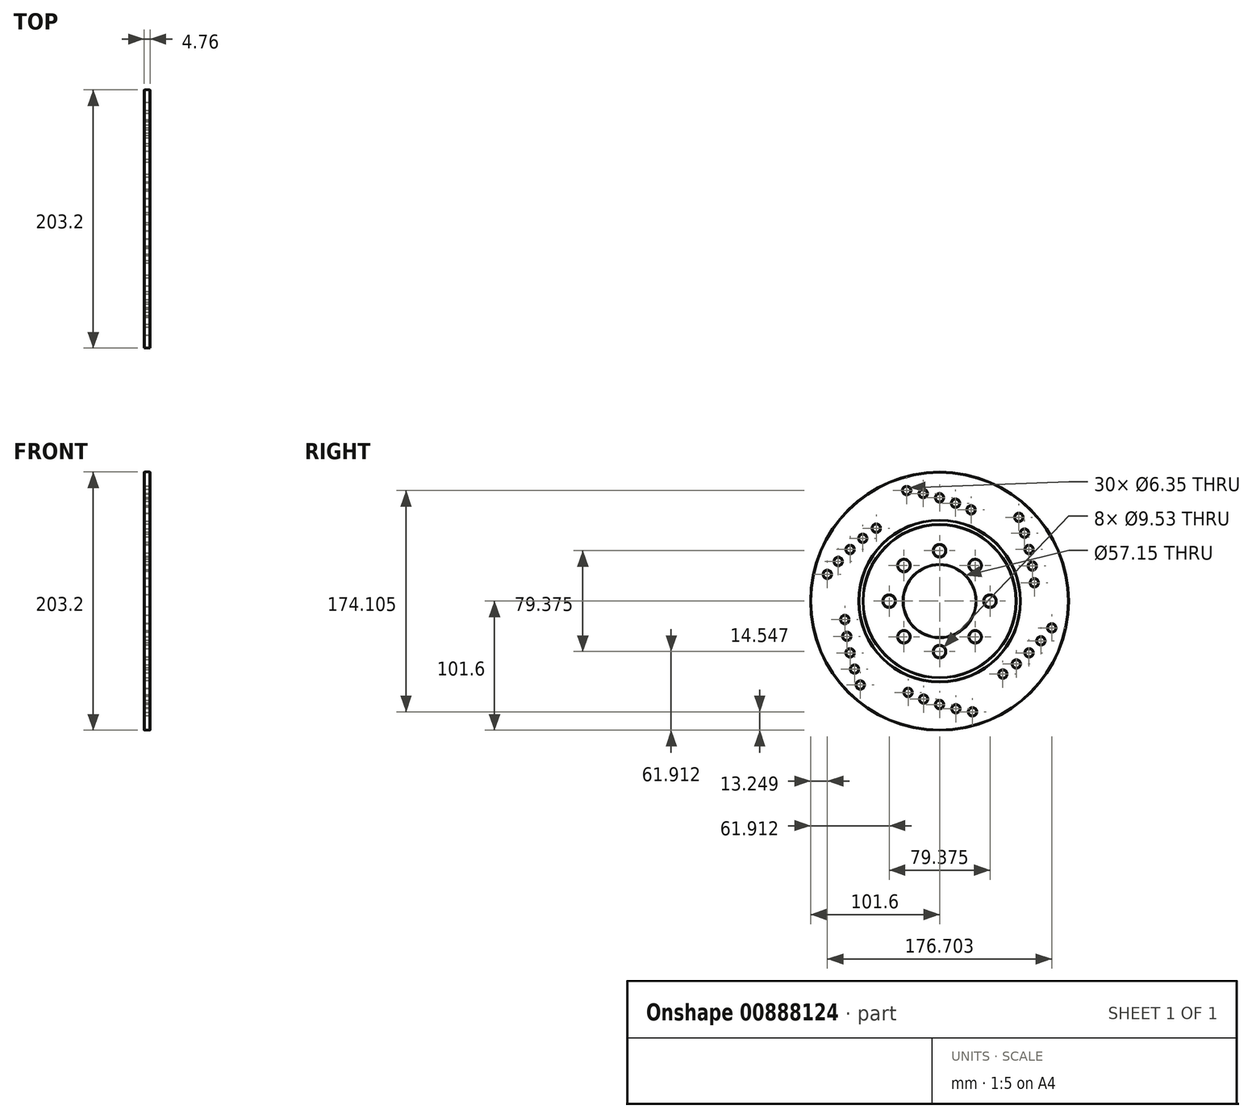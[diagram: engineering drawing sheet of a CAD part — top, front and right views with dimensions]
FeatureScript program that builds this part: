
annotation { "Feature Type Name" : "Feature", "Feature Type Description" : "" }
export const myFeature = defineFeature(function(context is Context, id is Id, definition is map)
    precondition{}
    {
        {
            var Q0;
            Q0=qCreatedBy(makeId("Right.planeOp"),FACE);
            var sketch = newSketch(context, id + "F0", { "sketchPlane" : qUnion([Q0])});
            skCircle(sketch, "E0", {"center": v(0, 0) * mm, "radius": 28.58 * mm});
            skCircle(sketch, "E1", {"center": v(0, 0) * mm, "radius": 101.6 * mm});
            skLineSegment(sketch, "E2", {"start": v(0, 0) * mm, "end": v(0, 39.69) * mm, "construction": true});
            skCircle(sketch, "E3", {"center": v(0, 39.69) * mm, "radius": 4.76 * mm});
            skCircle(sketch, "E4.1.0", {"center": v(-28.06, 28.06) * mm, "radius": 4.76 * mm});
            skCircle(sketch, "E4.2.0", {"center": v(-39.69, 0) * mm, "radius": 4.76 * mm});
            skCircle(sketch, "E4.3.0", {"center": v(-28.06, -28.06) * mm, "radius": 4.76 * mm});
            skCircle(sketch, "E4.4.0", {"center": v(0, -39.69) * mm, "radius": 4.76 * mm});
            skCircle(sketch, "E4.5.0", {"center": v(28.06, -28.06) * mm, "radius": 4.76 * mm});
            skCircle(sketch, "E4.6.0", {"center": v(39.69, 0) * mm, "radius": 4.76 * mm});
            skCircle(sketch, "E4.7.0", {"center": v(28.06, 28.06) * mm, "radius": 4.76 * mm});
            skLineSegment(sketch, "E5", {"start": v(0, 39.69) * mm, "end": v(0, 81.36) * mm, "construction": true});
            skArc(sketch, "E6", {"start": v(24.78, 71.84) * mm, "mid": v(0, 81.36) * mm, "end": v(-25.92, 87.05) * mm, "construction": true});
            skCircle(sketch, "E7", {"center": v(-25.92, 87.05) * mm, "radius": 3.18 * mm});
            skCircle(sketch, "E8", {"center": v(24.78, 71.84) * mm, "radius": 3.18 * mm});
            skCircle(sketch, "E9", {"center": v(0, 81.36) * mm, "radius": 3.18 * mm});
            skCircle(sketch, "E10", {"center": v(-12.85, 84.7) * mm, "radius": 3.18 * mm});
            skCircle(sketch, "E11", {"center": v(12.57, 77.07) * mm, "radius": 3.18 * mm});
            skLineSegment(sketch, "E12", {"start": v(-25.92, 87.05) * mm, "end": v(-12.85, 84.7) * mm, "construction": true});
            skLineSegment(sketch, "E13", {"start": v(-12.85, 84.7) * mm, "end": v(0, 81.36) * mm, "construction": true});
            skLineSegment(sketch, "E14", {"start": v(0, 81.36) * mm, "end": v(12.57, 77.07) * mm, "construction": true});
            skLineSegment(sketch, "E15", {"start": v(0, 0) * mm, "end": v(-50.8, -87.99) * mm, "construction": true});
            skCircle(sketch, "E16.1.0", {"center": v(-88.35, 21.08) * mm, "radius": 3.18 * mm});
            skCircle(sketch, "E16.1.1", {"center": v(-79.77, 31.21) * mm, "radius": 3.18 * mm});
            skCircle(sketch, "E16.1.2", {"center": v(-70.46, 40.68) * mm, "radius": 3.18 * mm});
            skCircle(sketch, "E16.1.3", {"center": v(-60.46, 49.42) * mm, "radius": 3.18 * mm});
            skCircle(sketch, "E16.1.4", {"center": v(-49.83, 57.38) * mm, "radius": 3.18 * mm});
            skCircle(sketch, "E16.2.0", {"center": v(-62.43, -65.98) * mm, "radius": 3.18 * mm});
            skCircle(sketch, "E16.2.1", {"center": v(-66.92, -53.48) * mm, "radius": 3.18 * mm});
            skCircle(sketch, "E16.2.2", {"center": v(-70.46, -40.68) * mm, "radius": 3.18 * mm});
            skCircle(sketch, "E16.2.3", {"center": v(-73.02, -27.65) * mm, "radius": 3.18 * mm});
            skCircle(sketch, "E16.2.4", {"center": v(-74.6, -14.46) * mm, "radius": 3.18 * mm});
            skCircle(sketch, "E16.3.0", {"center": v(25.92, -87.05) * mm, "radius": 3.18 * mm});
            skCircle(sketch, "E16.3.1", {"center": v(12.85, -84.7) * mm, "radius": 3.18 * mm});
            skCircle(sketch, "E16.3.2", {"center": v(0, -81.36) * mm, "radius": 3.18 * mm});
            skCircle(sketch, "E16.3.3", {"center": v(-12.57, -77.07) * mm, "radius": 3.18 * mm});
            skCircle(sketch, "E16.3.4", {"center": v(-24.78, -71.84) * mm, "radius": 3.18 * mm});
            skCircle(sketch, "E16.4.0", {"center": v(88.35, -21.08) * mm, "radius": 3.18 * mm});
            skCircle(sketch, "E16.4.1", {"center": v(79.77, -31.21) * mm, "radius": 3.18 * mm});
            skCircle(sketch, "E16.4.2", {"center": v(70.46, -40.68) * mm, "radius": 3.18 * mm});
            skCircle(sketch, "E16.4.3", {"center": v(60.46, -49.42) * mm, "radius": 3.18 * mm});
            skCircle(sketch, "E16.4.4", {"center": v(49.83, -57.38) * mm, "radius": 3.18 * mm});
            skCircle(sketch, "E16.5.0", {"center": v(62.43, 65.98) * mm, "radius": 3.18 * mm});
            skCircle(sketch, "E16.5.1", {"center": v(66.92, 53.48) * mm, "radius": 3.18 * mm});
            skCircle(sketch, "E16.5.2", {"center": v(70.46, 40.68) * mm, "radius": 3.18 * mm});
            skCircle(sketch, "E16.5.3", {"center": v(73.02, 27.65) * mm, "radius": 3.18 * mm});
            skCircle(sketch, "E16.5.4", {"center": v(74.6, 14.46) * mm, "radius": 3.18 * mm});
            skSolve(sketch);
        }
        {
            var Q0;
            Q0 = qSketchRegion(id + "F0", true);
            extrude(context, id + "F1", {"entities" : qUnion([Q0]), "depth" : 4.76 * mm, "offsetDistance" : 25.4 * mm, "symmetric" : true});
        }
        {
            var Q0;
            Q0=qCreatedBy(makeId("Front.planeOp"),FACE);
            var sketch = newSketch(context, id + "F2", { "sketchPlane" : qUnion([Q0])});
            skLineSegment(sketch, "E17", {"start": v(0, 0) * mm, "end": v(-25.4, 0) * mm, "construction": true});
            skLineSegment(sketch, "E18.bottom", {"start": v(-2.13, 63.5) * mm, "end": v(-25.4, 63.5) * mm});
            skLineSegment(sketch, "E18.top", {"start": v(-2.13, 60.33) * mm, "end": v(-25.4, 60.33) * mm});
            skLineSegment(sketch, "E18.left", {"start": v(-2.13, 63.5) * mm, "end": v(-2.13, 60.33) * mm});
            skLineSegment(sketch, "E18.right", {"start": v(-25.4, 63.5) * mm, "end": v(-25.4, 60.33) * mm});
            skLineSegment(sketch, "E19", {"start": v(0, 0) * mm, "end": v(0, 25.4) * mm, "construction": true});
            skLineSegment(sketch, "E20.MirrorCS", {"start": v(2.13, 63.5) * mm, "end": v(2.13, 60.33) * mm});
            skLineSegment(sketch, "E21.MirrorCS", {"start": v(2.13, 63.5) * mm, "end": v(25.4, 63.5) * mm});
            skLineSegment(sketch, "E22.MirrorCS", {"start": v(25.4, 63.5) * mm, "end": v(25.4, 60.33) * mm});
            skLineSegment(sketch, "E23.MirrorCS", {"start": v(2.13, 60.33) * mm, "end": v(25.4, 60.33) * mm});
            skSolve(sketch);
        }
        {
            var Q0;
            Q0=makeQuery(id+"F2.imprint","IMPRINT",FACE,{"disambiguationData":[TD([[makeQuery(id+"F2.imprint","IMPRINT",EDGE,{"derivedFrom":sQuery(id+"F2.wireOp",EDGE,"E18.bottom")}),1.0]])]});
            var Q1;
            Q1=makeQuery(id+"F2.imprint","IMPRINT",FACE,{"disambiguationData":[TD([[makeQuery(id+"F2.imprint","IMPRINT",EDGE,{"derivedFrom":sQuery(id+"F2.wireOp",EDGE,"E20.MirrorCS")}),1.0]])]});
            var Q2;
            Q2=sQuery(id+"F2.wireOp",EDGE,"E17");
            revolve(context, id + "F3", {"operationType" : NewBodyOperationType.REMOVE, "surfaceOperationType" : NewSurfaceOperationType.NEW, "entities" : qUnion([Q0, Q1]), "axis" : qUnion([Q2]), "revolveType" : RevolveType.FULL, "oppositeDirection" : true});
        }
        {
            var Q0;
            {var subQ0=sQuery(id+"F0.wireOp",EDGE,"E16.4.0");var subQ1=sQuery(id+"F0.wireOp",EDGE,"E16.3.4");var subQ2=sQuery(id+"F0.wireOp",EDGE,"E16.3.3");var subQ3=sQuery(id+"F0.wireOp",EDGE,"E16.3.2");var subQ4=sQuery(id+"F0.wireOp",EDGE,"E16.3.1");var subQ5=sQuery(id+"F0.wireOp",EDGE,"E16.3.0");var subQ6=sQuery(id+"F0.wireOp",EDGE,"E16.2.3");var subQ7=sQuery(id+"F0.wireOp",EDGE,"E16.2.2");var subQ8=sQuery(id+"F0.wireOp",EDGE,"E16.2.1");var subQ9=sQuery(id+"F0.wireOp",EDGE,"E16.2.0");var subQ10=sQuery(id+"F0.wireOp",EDGE,"E16.1.4");var subQ11=sQuery(id+"F0.wireOp",EDGE,"E9");var subQ12=sQuery(id+"F0.wireOp",EDGE,"E16.2.4");var subQ13=sQuery(id+"F0.wireOp",EDGE,"E1");var subQ14=sQuery(id+"F0.wireOp",EDGE,"E7");var subQ15=sQuery(id+"F0.wireOp",EDGE,"E8");var subQ16=sQuery(id+"F0.wireOp",EDGE,"E10");var subQ17=sQuery(id+"F0.wireOp",EDGE,"E11");var subQ18=sQuery(id+"F0.wireOp",EDGE,"E16.1.0");var subQ19=sQuery(id+"F0.wireOp",EDGE,"E16.1.1");var subQ20=sQuery(id+"F0.wireOp",EDGE,"E16.1.2");var subQ21=sQuery(id+"F0.wireOp",EDGE,"E16.1.3");var subQ22=sQuery(id+"F0.wireOp",EDGE,"E16.4.1");var subQ23=sQuery(id+"F0.wireOp",EDGE,"E16.4.2");var subQ24=sQuery(id+"F0.wireOp",EDGE,"E16.4.3");var subQ25=sQuery(id+"F0.wireOp",EDGE,"E16.4.4");var subQ26=sQuery(id+"F0.wireOp",EDGE,"E16.5.0");var subQ27=sQuery(id+"F0.wireOp",EDGE,"E16.5.1");var subQ28=sQuery(id+"F0.wireOp",EDGE,"E16.5.2");var subQ29=sQuery(id+"F0.wireOp",EDGE,"E16.5.3");var subQ30=sQuery(id+"F0.wireOp",EDGE,"E16.5.4");Q0=makeQuery(id+"F3.boolean.opBoolean","SPLIT",FACE,{"disambiguationData":[TD([makeQuery(id+"F1.opExtrude","SWEPT_FACE",FACE,{"disambiguationData":[OSD([subQ13])]})])],"derivedFrom":makeQuery(id+"F1.opExtrude","CAP_FACE",FACE,{"disambiguationData":[OSD([sQuery(id+"F0.wireOp",EDGE,"E0"),subQ13,sQuery(id+"F0.wireOp",EDGE,"E3"),sQuery(id+"F0.wireOp",EDGE,"E4.1.0"),sQuery(id+"F0.wireOp",EDGE,"E4.2.0"),sQuery(id+"F0.wireOp",EDGE,"E4.3.0"),sQuery(id+"F0.wireOp",EDGE,"E4.4.0"),sQuery(id+"F0.wireOp",EDGE,"E4.5.0"),sQuery(id+"F0.wireOp",EDGE,"E4.6.0"),sQuery(id+"F0.wireOp",EDGE,"E4.7.0"),subQ14,subQ15,subQ11,subQ16,subQ17,subQ18,subQ19,subQ20,subQ21,subQ10,subQ9,subQ8,subQ7,subQ6,subQ12,subQ5,subQ4,subQ3,subQ2,subQ1,subQ0,subQ22,subQ23,subQ24,subQ25,subQ26,subQ27,subQ28,subQ29,subQ30])],"isStart":true})});}
            var Q1;
            {var subQ0=sQuery(id+"F0.wireOp",EDGE,"E4.2.0");var subQ1=sQuery(id+"F0.wireOp",EDGE,"E3");var subQ2=sQuery(id+"F0.wireOp",EDGE,"E4.1.0");var subQ3=sQuery(id+"F0.wireOp",EDGE,"E0");var subQ4=sQuery(id+"F0.wireOp",EDGE,"E4.7.0");var subQ5=sQuery(id+"F0.wireOp",EDGE,"E4.3.0");var subQ6=sQuery(id+"F0.wireOp",EDGE,"E4.4.0");var subQ7=sQuery(id+"F0.wireOp",EDGE,"E4.5.0");var subQ8=sQuery(id+"F0.wireOp",EDGE,"E4.6.0");Q1=makeQuery(id+"F3.boolean.opBoolean","SPLIT",FACE,{"disambiguationData":[TD([makeQuery(id+"F1.opExtrude","SWEPT_FACE",FACE,{"disambiguationData":[OSD([subQ3])]})])],"derivedFrom":makeQuery(id+"F1.opExtrude","CAP_FACE",FACE,{"disambiguationData":[OSD([subQ3,sQuery(id+"F0.wireOp",EDGE,"E1"),subQ1,subQ2,subQ0,subQ5,subQ6,subQ7,subQ8,subQ4,sQuery(id+"F0.wireOp",EDGE,"E7"),sQuery(id+"F0.wireOp",EDGE,"E8"),sQuery(id+"F0.wireOp",EDGE,"E9"),sQuery(id+"F0.wireOp",EDGE,"E10"),sQuery(id+"F0.wireOp",EDGE,"E11"),sQuery(id+"F0.wireOp",EDGE,"E16.1.0"),sQuery(id+"F0.wireOp",EDGE,"E16.1.1"),sQuery(id+"F0.wireOp",EDGE,"E16.1.2"),sQuery(id+"F0.wireOp",EDGE,"E16.1.3"),sQuery(id+"F0.wireOp",EDGE,"E16.1.4"),sQuery(id+"F0.wireOp",EDGE,"E16.2.0"),sQuery(id+"F0.wireOp",EDGE,"E16.2.1"),sQuery(id+"F0.wireOp",EDGE,"E16.2.2"),sQuery(id+"F0.wireOp",EDGE,"E16.2.3"),sQuery(id+"F0.wireOp",EDGE,"E16.2.4"),sQuery(id+"F0.wireOp",EDGE,"E16.3.0"),sQuery(id+"F0.wireOp",EDGE,"E16.3.1"),sQuery(id+"F0.wireOp",EDGE,"E16.3.2"),sQuery(id+"F0.wireOp",EDGE,"E16.3.3"),sQuery(id+"F0.wireOp",EDGE,"E16.3.4"),sQuery(id+"F0.wireOp",EDGE,"E16.4.0"),sQuery(id+"F0.wireOp",EDGE,"E16.4.1"),sQuery(id+"F0.wireOp",EDGE,"E16.4.2"),sQuery(id+"F0.wireOp",EDGE,"E16.4.3"),sQuery(id+"F0.wireOp",EDGE,"E16.4.4"),sQuery(id+"F0.wireOp",EDGE,"E16.5.0"),sQuery(id+"F0.wireOp",EDGE,"E16.5.1"),sQuery(id+"F0.wireOp",EDGE,"E16.5.2"),sQuery(id+"F0.wireOp",EDGE,"E16.5.3"),sQuery(id+"F0.wireOp",EDGE,"E16.5.4")])],"isStart":true})});}
            var Q2;
            {var subQ0=sQuery(id+"F0.wireOp",EDGE,"E4.2.0");var subQ1=sQuery(id+"F0.wireOp",EDGE,"E3");var subQ2=sQuery(id+"F0.wireOp",EDGE,"E4.1.0");var subQ3=sQuery(id+"F0.wireOp",EDGE,"E0");var subQ4=sQuery(id+"F0.wireOp",EDGE,"E4.7.0");var subQ5=sQuery(id+"F0.wireOp",EDGE,"E4.3.0");var subQ6=sQuery(id+"F0.wireOp",EDGE,"E4.4.0");var subQ7=sQuery(id+"F0.wireOp",EDGE,"E4.5.0");var subQ8=sQuery(id+"F0.wireOp",EDGE,"E4.6.0");Q2=makeQuery(id+"F3.boolean.opBoolean","SPLIT",FACE,{"disambiguationData":[TD([makeQuery(id+"F1.opExtrude","SWEPT_FACE",FACE,{"disambiguationData":[OSD([subQ3])]})])],"derivedFrom":makeQuery(id+"F1.opExtrude","CAP_FACE",FACE,{"disambiguationData":[OSD([subQ3,sQuery(id+"F0.wireOp",EDGE,"E1"),subQ1,subQ2,subQ0,subQ5,subQ6,subQ7,subQ8,subQ4,sQuery(id+"F0.wireOp",EDGE,"E7"),sQuery(id+"F0.wireOp",EDGE,"E8"),sQuery(id+"F0.wireOp",EDGE,"E9"),sQuery(id+"F0.wireOp",EDGE,"E10"),sQuery(id+"F0.wireOp",EDGE,"E11"),sQuery(id+"F0.wireOp",EDGE,"E16.1.0"),sQuery(id+"F0.wireOp",EDGE,"E16.1.1"),sQuery(id+"F0.wireOp",EDGE,"E16.1.2"),sQuery(id+"F0.wireOp",EDGE,"E16.1.3"),sQuery(id+"F0.wireOp",EDGE,"E16.1.4"),sQuery(id+"F0.wireOp",EDGE,"E16.2.0"),sQuery(id+"F0.wireOp",EDGE,"E16.2.1"),sQuery(id+"F0.wireOp",EDGE,"E16.2.2"),sQuery(id+"F0.wireOp",EDGE,"E16.2.3"),sQuery(id+"F0.wireOp",EDGE,"E16.2.4"),sQuery(id+"F0.wireOp",EDGE,"E16.3.0"),sQuery(id+"F0.wireOp",EDGE,"E16.3.1"),sQuery(id+"F0.wireOp",EDGE,"E16.3.2"),sQuery(id+"F0.wireOp",EDGE,"E16.3.3"),sQuery(id+"F0.wireOp",EDGE,"E16.3.4"),sQuery(id+"F0.wireOp",EDGE,"E16.4.0"),sQuery(id+"F0.wireOp",EDGE,"E16.4.1"),sQuery(id+"F0.wireOp",EDGE,"E16.4.2"),sQuery(id+"F0.wireOp",EDGE,"E16.4.3"),sQuery(id+"F0.wireOp",EDGE,"E16.4.4"),sQuery(id+"F0.wireOp",EDGE,"E16.5.0"),sQuery(id+"F0.wireOp",EDGE,"E16.5.1"),sQuery(id+"F0.wireOp",EDGE,"E16.5.2"),sQuery(id+"F0.wireOp",EDGE,"E16.5.3"),sQuery(id+"F0.wireOp",EDGE,"E16.5.4")])],"isStart":false})});}
            var Q3;
            {var subQ0=sQuery(id+"F0.wireOp",EDGE,"E16.4.0");var subQ1=sQuery(id+"F0.wireOp",EDGE,"E16.3.4");var subQ2=sQuery(id+"F0.wireOp",EDGE,"E16.3.3");var subQ3=sQuery(id+"F0.wireOp",EDGE,"E16.3.2");var subQ4=sQuery(id+"F0.wireOp",EDGE,"E16.3.1");var subQ5=sQuery(id+"F0.wireOp",EDGE,"E16.3.0");var subQ6=sQuery(id+"F0.wireOp",EDGE,"E16.2.3");var subQ7=sQuery(id+"F0.wireOp",EDGE,"E16.2.2");var subQ8=sQuery(id+"F0.wireOp",EDGE,"E16.2.1");var subQ9=sQuery(id+"F0.wireOp",EDGE,"E16.2.0");var subQ10=sQuery(id+"F0.wireOp",EDGE,"E16.1.4");var subQ11=sQuery(id+"F0.wireOp",EDGE,"E9");var subQ12=sQuery(id+"F0.wireOp",EDGE,"E16.2.4");var subQ13=sQuery(id+"F0.wireOp",EDGE,"E1");var subQ14=sQuery(id+"F0.wireOp",EDGE,"E7");var subQ15=sQuery(id+"F0.wireOp",EDGE,"E8");var subQ16=sQuery(id+"F0.wireOp",EDGE,"E10");var subQ17=sQuery(id+"F0.wireOp",EDGE,"E11");var subQ18=sQuery(id+"F0.wireOp",EDGE,"E16.1.0");var subQ19=sQuery(id+"F0.wireOp",EDGE,"E16.1.1");var subQ20=sQuery(id+"F0.wireOp",EDGE,"E16.1.2");var subQ21=sQuery(id+"F0.wireOp",EDGE,"E16.1.3");var subQ22=sQuery(id+"F0.wireOp",EDGE,"E16.4.1");var subQ23=sQuery(id+"F0.wireOp",EDGE,"E16.4.2");var subQ24=sQuery(id+"F0.wireOp",EDGE,"E16.4.3");var subQ25=sQuery(id+"F0.wireOp",EDGE,"E16.4.4");var subQ26=sQuery(id+"F0.wireOp",EDGE,"E16.5.0");var subQ27=sQuery(id+"F0.wireOp",EDGE,"E16.5.1");var subQ28=sQuery(id+"F0.wireOp",EDGE,"E16.5.2");var subQ29=sQuery(id+"F0.wireOp",EDGE,"E16.5.3");var subQ30=sQuery(id+"F0.wireOp",EDGE,"E16.5.4");Q3=makeQuery(id+"F3.boolean.opBoolean","SPLIT",FACE,{"disambiguationData":[TD([makeQuery(id+"F1.opExtrude","SWEPT_FACE",FACE,{"disambiguationData":[OSD([subQ13])]})])],"derivedFrom":makeQuery(id+"F1.opExtrude","CAP_FACE",FACE,{"disambiguationData":[OSD([sQuery(id+"F0.wireOp",EDGE,"E0"),subQ13,sQuery(id+"F0.wireOp",EDGE,"E3"),sQuery(id+"F0.wireOp",EDGE,"E4.1.0"),sQuery(id+"F0.wireOp",EDGE,"E4.2.0"),sQuery(id+"F0.wireOp",EDGE,"E4.3.0"),sQuery(id+"F0.wireOp",EDGE,"E4.4.0"),sQuery(id+"F0.wireOp",EDGE,"E4.5.0"),sQuery(id+"F0.wireOp",EDGE,"E4.6.0"),sQuery(id+"F0.wireOp",EDGE,"E4.7.0"),subQ14,subQ15,subQ11,subQ16,subQ17,subQ18,subQ19,subQ20,subQ21,subQ10,subQ9,subQ8,subQ7,subQ6,subQ12,subQ5,subQ4,subQ3,subQ2,subQ1,subQ0,subQ22,subQ23,subQ24,subQ25,subQ26,subQ27,subQ28,subQ29,subQ30])],"isStart":false})});}
            chamfer(context, id + "F4", {"entities" : qUnion([Q0, Q1, Q2, Q3]), "width" : 0.25 * mm, "tangentPropagation" : true});
        }
    });
